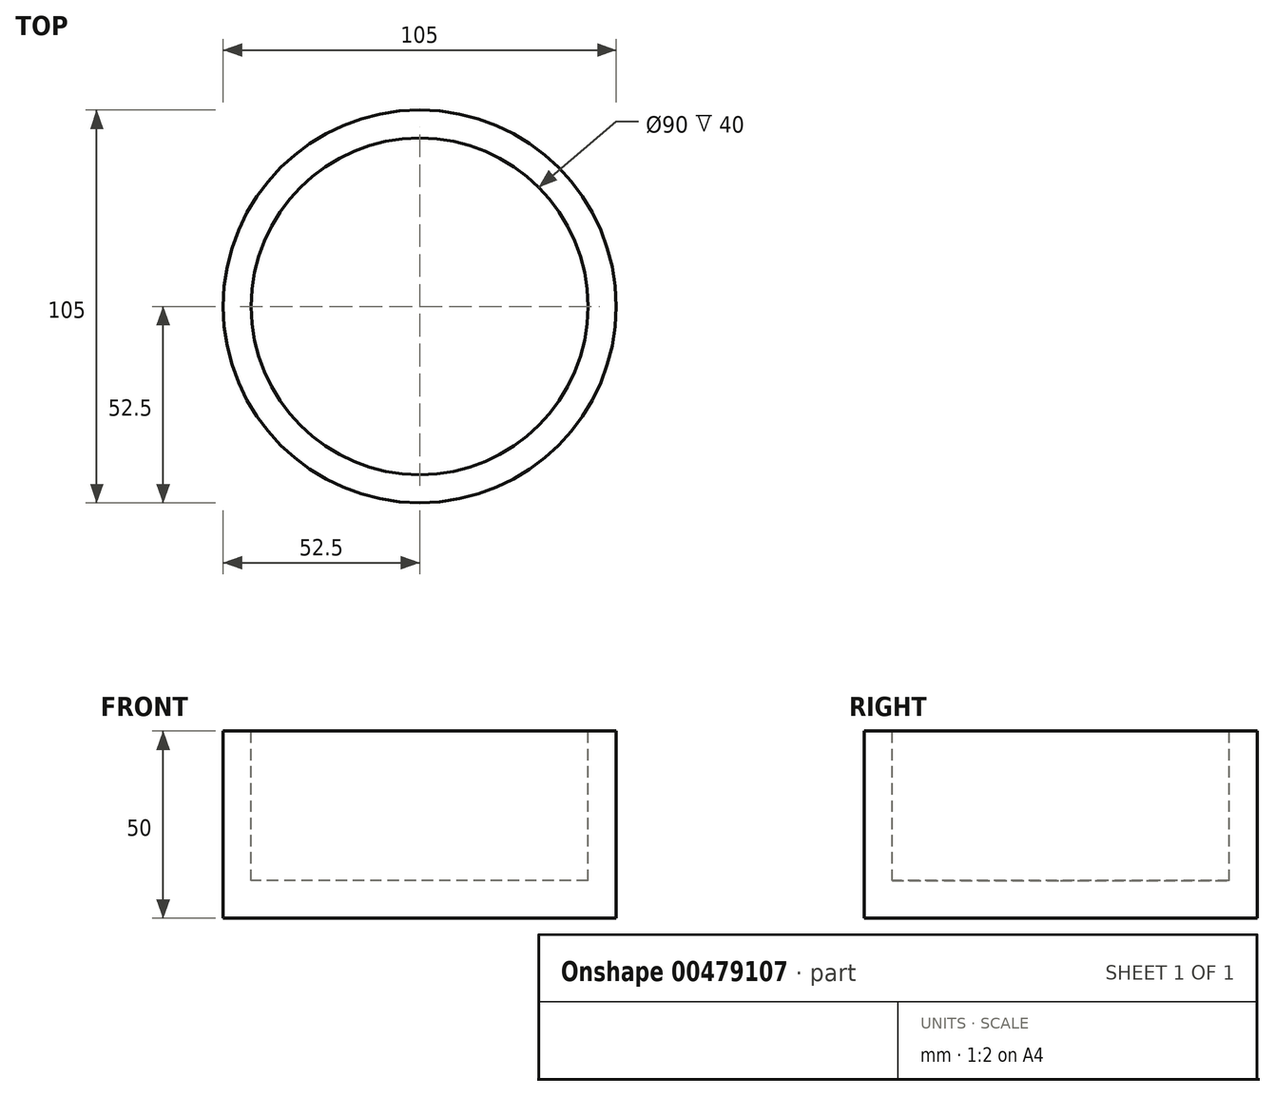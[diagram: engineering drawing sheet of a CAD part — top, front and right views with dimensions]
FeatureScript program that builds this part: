
annotation { "Feature Type Name" : "Feature", "Feature Type Description" : "" }
export const myFeature = defineFeature(function(context is Context, id is Id, definition is map)
    precondition{}
    {
        {
            var Q0;
            Q0=qCreatedBy(makeId("Top.planeOp"),FACE);
            var sketch = newSketch(context, id + "F0", { "sketchPlane" : qUnion([Q0])});
            skCircle(sketch, "E0", {"center": v(0, 0) * mm, "radius": 52.5 * mm});
            skSolve(sketch);
        }
        {
            var Q0;
            Q0=makeQuery(id+"F0.imprint","IMPRINT",FACE,{"disambiguationData":[TD([[makeQuery(id+"F0.imprint","IMPRINT",EDGE,{"derivedFrom":sQuery(id+"F0.wireOp",EDGE,"E0")}),1.0]])]});
            extrude(context, id + "F1", {"entities" : qUnion([Q0]), "depth" : 50 * mm, "offsetDistance" : 25 * mm});
        }
        {
            var Q0;
            Q0=makeQuery(id+"F1.opExtrude","CAP_FACE",FACE,{"disambiguationData":[OSD([sQuery(id+"F0.wireOp",EDGE,"E0")])],"isStart":false});
            var sketch = newSketch(context, id + "F2", { "sketchPlane" : qUnion([Q0])});
            skCircle(sketch, "E1", {"center": v(0, 0) * mm, "radius": 45 * mm});
            skSolve(sketch);
        }
        {
            var Q0;
            Q0=qSketchRegion(id+"F2",true);
            extrude(context, id + "F3", {"entities" : qUnion([Q0]), "operationType" : NewBodyOperationType.REMOVE, "oppositeDirection" : true, "depth" : 40 * mm, "offsetDistance" : 25 * mm});
        }
    });
